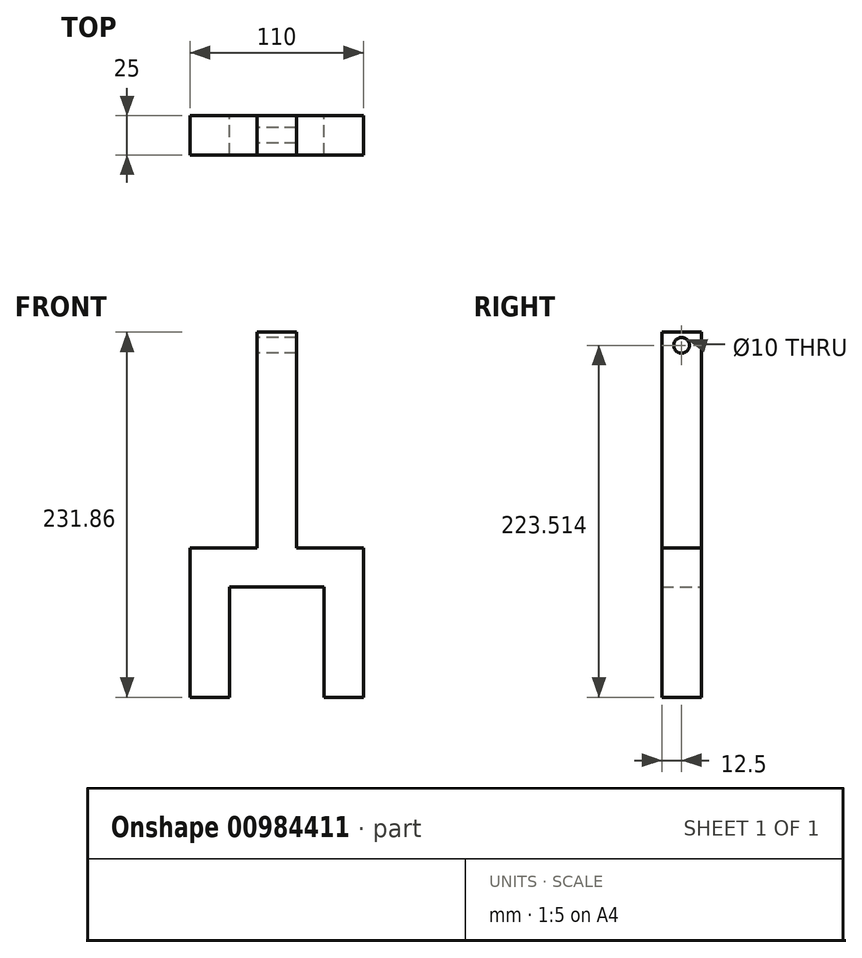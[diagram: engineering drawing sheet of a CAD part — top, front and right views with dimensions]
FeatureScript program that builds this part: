
annotation { "Feature Type Name" : "Feature", "Feature Type Description" : "" }
export const myFeature = defineFeature(function(context is Context, id is Id, definition is map)
    precondition{}
    {
        {
            var Q0;
            Q0=qCreatedBy(makeId("Front.planeOp"),FACE);
            var sketch = newSketch(context, id + "F0", { "sketchPlane" : qUnion([Q0])});
            skLineSegment(sketch, "E0.bottom", {"start": v(-62.83, 98.3) * mm, "end": v(-37.83, 98.3) * mm});
            skLineSegment(sketch, "E0.top", {"start": v(-62.83, -38.66) * mm, "end": v(-37.83, -38.66) * mm});
            skLineSegment(sketch, "E0.left", {"start": v(-62.83, 98.3) * mm, "end": v(-62.83, -38.66) * mm});
            skLineSegment(sketch, "E0.right", {"start": v(-37.83, 98.3) * mm, "end": v(-37.83, -38.66) * mm});
            skLineSegment(sketch, "E1", {"start": v(-50.33, -38.66) * mm, "end": v(-50.33, -51.16) * mm});
            skLineSegment(sketch, "E2.bottom", {"start": v(-105.33, -38.66) * mm, "end": v(4.67, -38.66) * mm});
            skLineSegment(sketch, "E2.top", {"start": v(-105.33, -63.66) * mm, "end": v(4.67, -63.66) * mm});
            skLineSegment(sketch, "E2.left", {"start": v(-105.33, -38.66) * mm, "end": v(-105.33, -63.66) * mm});
            skLineSegment(sketch, "E2.right", {"start": v(4.67, -38.66) * mm, "end": v(4.67, -63.66) * mm});
            skPoint(sketch, "E2.middle", {"position": v(-50.33, -51.16) * mm});
            skLineSegment(sketch, "E3.bottom", {"start": v(-105.33, -63.66) * mm, "end": v(-80.33, -63.66) * mm});
            skLineSegment(sketch, "E3.top", {"start": v(-105.33, -133.56) * mm, "end": v(-80.33, -133.56) * mm});
            skLineSegment(sketch, "E3.left", {"start": v(-105.33, -63.66) * mm, "end": v(-105.33, -133.56) * mm});
            skLineSegment(sketch, "E3.right", {"start": v(-80.33, -63.66) * mm, "end": v(-80.33, -133.56) * mm});
            skLineSegment(sketch, "E4.MirrorCS", {"start": v(-20.33, -63.66) * mm, "end": v(-20.33, -133.56) * mm});
            skLineSegment(sketch, "E5.MirrorCS", {"start": v(4.67, -133.56) * mm, "end": v(-20.33, -133.56) * mm});
            skLineSegment(sketch, "E6.MirrorCS", {"start": v(4.67, -63.66) * mm, "end": v(4.67, -133.56) * mm});
            skSolve(sketch);
        }
        {
            var Q0;
            Q0 = qSketchRegion(id + "F0", true);
            extrude(context, id + "F1", {"entities" : qUnion([Q0]), "depth" : 25 * mm, "offsetDistance" : 25 * mm});
        }
        {
            var Q0;
            Q0=makeQuery(id+"F1.opExtrude","SWEPT_FACE",FACE,{"disambiguationData":[OSD([sQuery(id+"F0.wireOp",EDGE,"E0.left")])]});
            var sketch = newSketch(context, id + "F2", { "sketchPlane" : qUnion([Q0])});
            skLineSegment(sketch, "E7", {"start": v(12.5, 98.3) * mm, "end": v(12.5, 89.95) * mm});
            skCircle(sketch, "E8", {"center": v(12.5, 89.95) * mm, "radius": 5 * mm});
            skSolve(sketch);
        }
        {
            var Q0;
            Q0 = qSketchRegion(id + "F2", true);
            extrude(context, id + "F3", {"entities" : qUnion([Q0]), "operationType" : NewBodyOperationType.REMOVE, "oppositeDirection" : true, "depth" : 50 * mm, "offsetDistance" : 25 * mm});
        }
    });
